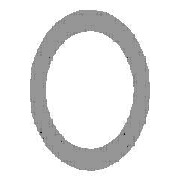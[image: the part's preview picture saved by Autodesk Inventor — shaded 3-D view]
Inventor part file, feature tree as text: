
AUTODESK INVENTOR PART (.ipt)
format: ipt  version: 2013 (Build 170138000, 138)  size: 138,240 bytes
history: native  units: mm (DEFAULTED — no unit token found)
features: plane x6, sketch x6, other x4, extrude x3
ambient origin geometry x8: Origin, YZ Plane, XZ Plane, XY Plane, X Axis, Y Axis, Z Axis, Center Point
bodies: Solid1 (feature_tree), Body (feature_tree)
feature tree (19):
  parser-record x1  (decoder bookkeeping rows leaked as tree rows — omitted from the tree; the rows remain in map.json)
  other  "Driven Length"
  other  "Start plane"
  other  "End plane"
  plane  "Work Plane4"
  plane  "Work Plane5"
  plane  "Work Plane6"
  extrude  "Extrusion2"  Depth=3.3782mm
  plane  "Work Plane7"
  extrude  "Extrusion3"  TaperAngle=0.0deg  [1 undecoded]
  plane  "Work Plane8"
  extrude  "Extrusion4"  TaperAngle=90.0deg  [1 undecoded]
  sketch  "Sketch"  dims[d10=38.1mm d11=0.0mm d12=6.35mm d13=38.1mm d14=0.0mm d15=16.7005mm]
  sketch  "Sketch3"  dims[d0=33.401mm d1=3.3782mm]
  plane  "Work Plane3"
  sketch  "Sketch4"  dims[d2=800.1mm d3=0.0mm d4=-0.0mm]
  sketch  "Sketch5"  dims[d5=800.1mm d6=90.0deg]
  sketch  "Sketch6"  dims[d7=800.1mm]
  sketch  "Sketch7"  dims[d8=3.302mm d9=0.0mm]
note: 2 required parameter values undecoded (feature->parameter linkage not recoverable at this tier; creation-order binding heuristic only, values carry confidence <= 0.55)
